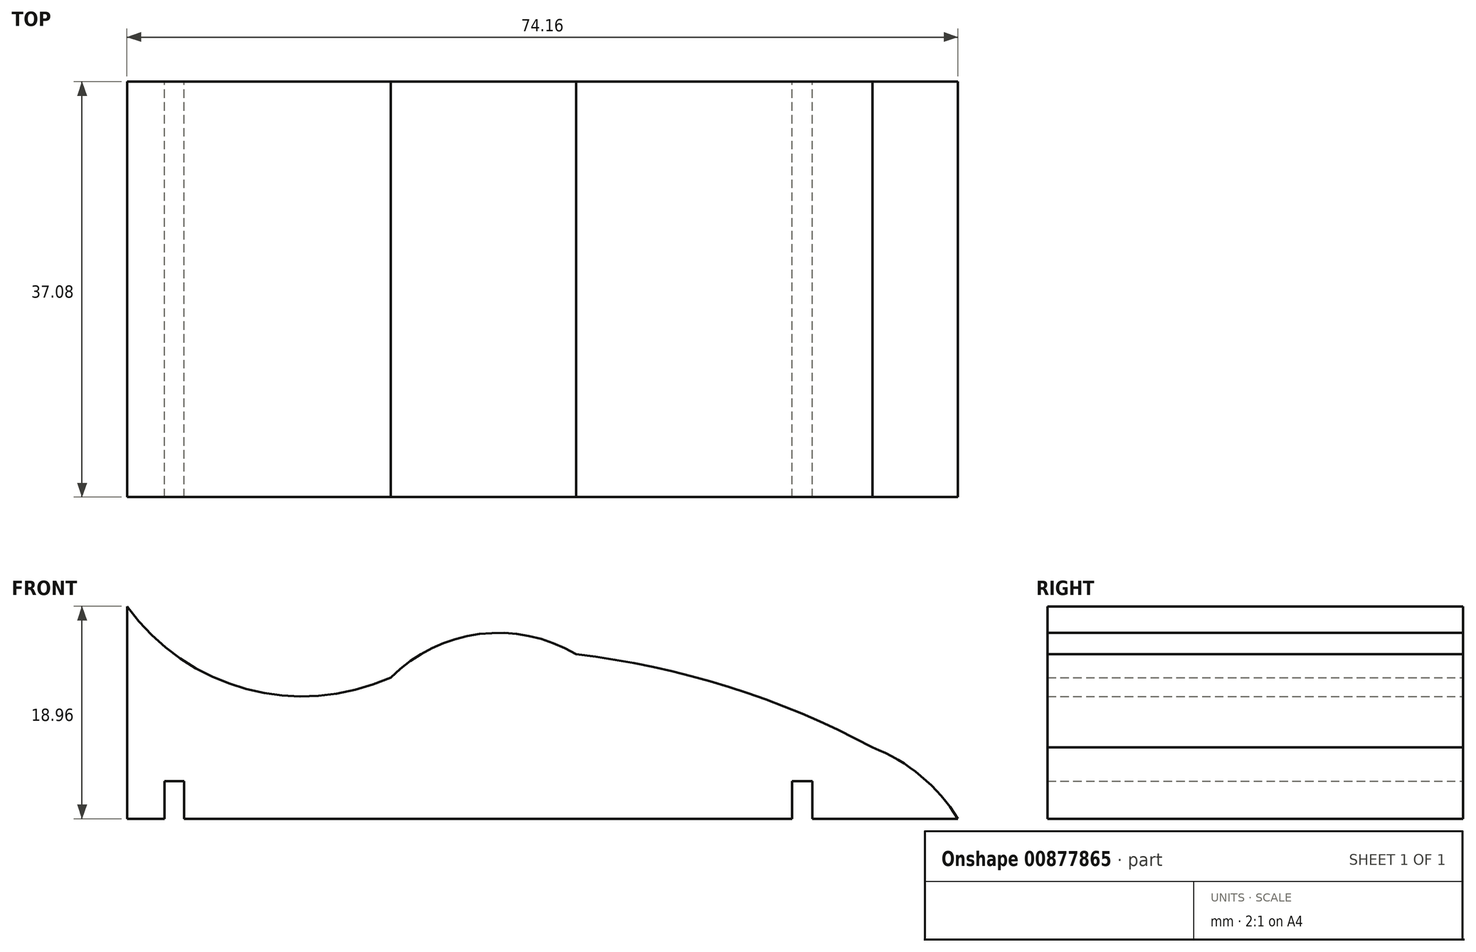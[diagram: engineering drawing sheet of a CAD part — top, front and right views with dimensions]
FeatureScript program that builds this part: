
annotation { "Feature Type Name" : "Feature", "Feature Type Description" : "" }
export const myFeature = defineFeature(function(context is Context, id is Id, definition is map)
    precondition{}
    {
        {
            var Q0;
            Q0=qCreatedBy(makeId("Front.planeOp"),FACE);
            var sketch = newSketch(context, id + "F0", { "sketchPlane" : qUnion([Q0])});
            skLineSegment(sketch, "E0", {"start": v(-10.6, 12.59) * mm, "end": v(-10.6, -6.37) * mm});
            skLineSegment(sketch, "E1", {"start": v(-10.6, -6.37) * mm, "end": v(-7.26, -6.37) * mm});
            skLineSegment(sketch, "E2", {"start": v(-7.26, -6.37) * mm, "end": v(-7.26, -3.02) * mm});
            skLineSegment(sketch, "E3", {"start": v(-7.26, -3.02) * mm, "end": v(-5.5, -3.02) * mm});
            skLineSegment(sketch, "E4", {"start": v(-5.5, -3.02) * mm, "end": v(-5.5, -6.37) * mm});
            skLineSegment(sketch, "E5", {"start": v(-5.5, -6.37) * mm, "end": v(48.76, -6.37) * mm});
            skLineSegment(sketch, "E6", {"start": v(48.76, -6.37) * mm, "end": v(48.76, -3.02) * mm});
            skLineSegment(sketch, "E7", {"start": v(48.76, -3.02) * mm, "end": v(50.55, -3.02) * mm});
            skLineSegment(sketch, "E8", {"start": v(50.55, -3.02) * mm, "end": v(50.55, -6.37) * mm});
            skLineSegment(sketch, "E9", {"start": v(50.55, -6.37) * mm, "end": v(60.48, -6.37) * mm});
            skArc(sketch, "E10", {"start": v(-10.6, 12.59) * mm, "mid": v(0.04, 5.22) * mm, "end": v(12.94, 6.23) * mm});
            skArc(sketch, "E11", {"start": v(29.48, 8.32) * mm, "mid": v(20.86, 10.11) * mm, "end": v(12.94, 6.23) * mm});
            skArc(sketch, "E12", {"start": v(55.92, 0) * mm, "mid": v(43.09, 5.4) * mm, "end": v(29.48, 8.32) * mm});
            skPoint(sketch, "E13.start.orphan", {"position": v(63.45, -3.02) * mm});
            skPoint(sketch, "E14.orphan", {"position": v(60.48, -0.4) * mm});
            skPoint(sketch, "E15.end.orphan", {"position": v(50.55, 0.47) * mm});
            skLineSegment(sketch, "E16", {"start": v(60.48, -6.37) * mm, "end": v(63.55, -6.37) * mm});
            skArc(sketch, "E17", {"start": v(63.55, -6.37) * mm, "mid": v(60.26, -2.56) * mm, "end": v(55.92, 0) * mm});
            skSolve(sketch);
        }
        {
            var Q0;
            Q0 = qSketchRegion(id + "F0", true);
            extrude(context, id + "F1", {"entities" : qUnion([Q0]), "depth" : 37.08 * mm, "offsetDistance" : 25.4 * mm});
        }
    });
